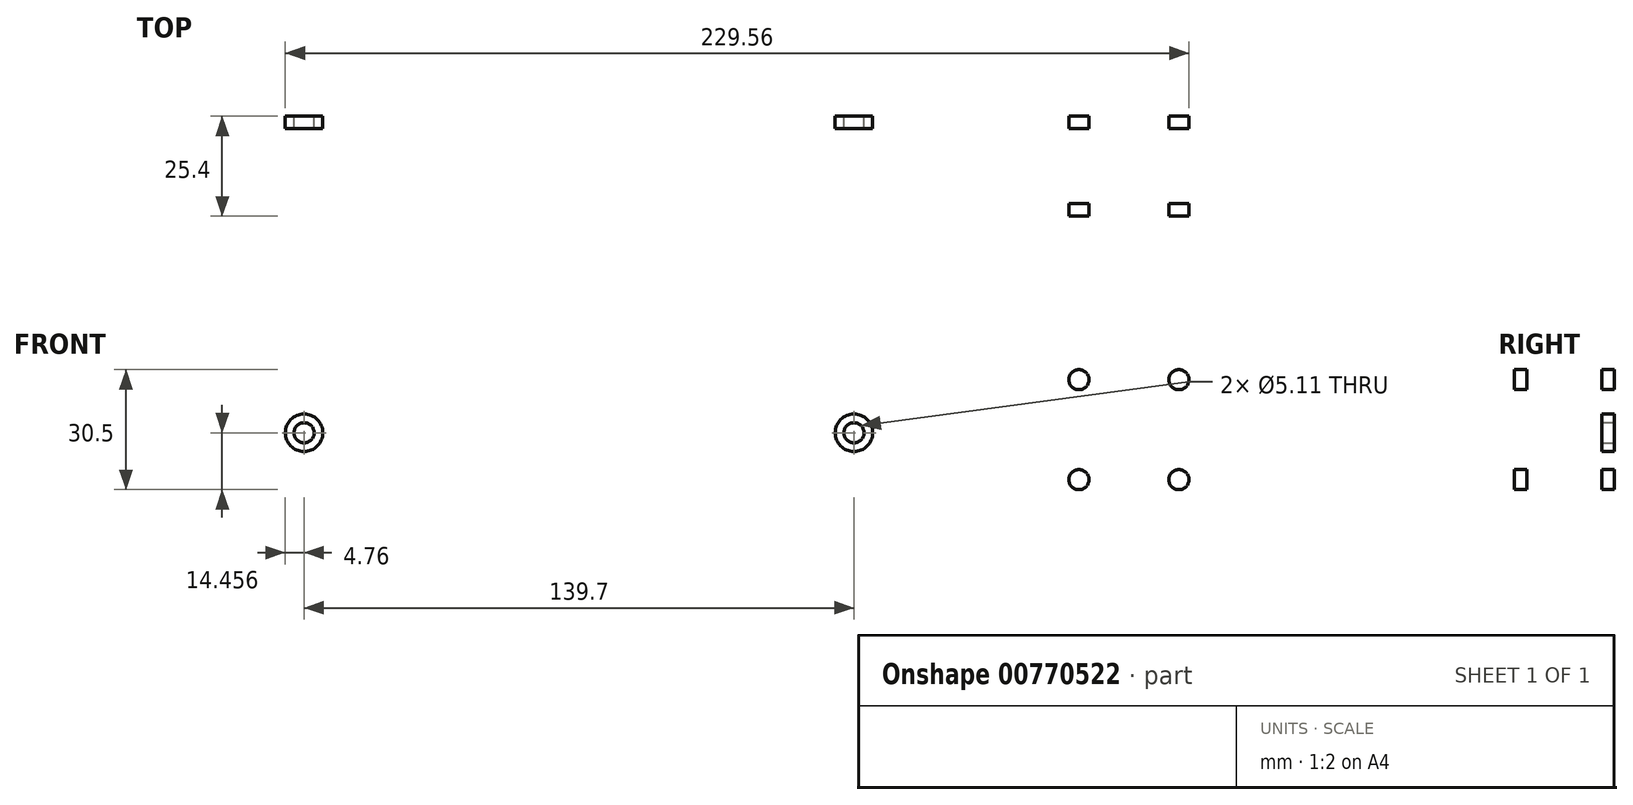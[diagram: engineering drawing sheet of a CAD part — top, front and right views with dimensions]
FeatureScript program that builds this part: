
annotation { "Feature Type Name" : "Feature", "Feature Type Description" : "" }
export const myFeature = defineFeature(function(context is Context, id is Id, definition is map)
    precondition{}
    {
        {
            var Q0;
            Q0=qCreatedBy(makeId("Front.planeOp"),FACE);
            var sketch = newSketch(context, id + "F0", { "sketchPlane" : qUnion([Q0])});
            skLineSegment(sketch, "E0.bottom", {"start": v(381, -25.4) * mm, "end": v(-381, -25.4) * mm});
            skLineSegment(sketch, "E0.top", {"start": v(381, 25.4) * mm, "end": v(-381, 25.4) * mm});
            skLineSegment(sketch, "E0.left", {"start": v(381, -25.4) * mm, "end": v(381, 25.4) * mm});
            skLineSegment(sketch, "E0.right", {"start": v(-381, -25.4) * mm, "end": v(-381, 25.4) * mm});
            skPoint(sketch, "E0.middle", {"position": v(0, 0) * mm});
            skLineSegment(sketch, "E1", {"start": v(-381, 0.8) * mm, "end": v(381, 0.8) * mm, "construction": true});
            skLineSegment(sketch, "E2", {"start": v(-381, -0.8) * mm, "end": v(381, -0.8) * mm, "construction": true});
            skLineSegment(sketch, "E3", {"start": v(0, 0.8) * mm, "end": v(0, -0.8) * mm, "construction": true});
            skCircle(sketch, "E4", {"center": v(-292.1, 0.8) * mm, "radius": 50.8 * mm, "construction": true});
            skCircle(sketch, "E5", {"center": v(292.1, 0.8) * mm, "radius": 50.8 * mm, "construction": true});
            skCircle(sketch, "E6", {"center": v(0, -0.8) * mm, "radius": 50.8 * mm, "construction": true});
            skLineSegment(sketch, "E7", {"start": v(-292.1, 0.8) * mm, "end": v(292.1, 0.8) * mm, "construction": true});
            skCircle(sketch, "E8", {"center": v(0, -0.8) * mm, "radius": 19.11 * mm});
            skCircle(sketch, "E9", {"center": v(-23.81, -0.8) * mm, "radius": 2.55 * mm});
            skCircle(sketch, "E10", {"center": v(23.81, -0.8) * mm, "radius": 2.55 * mm});
            skLineSegment(sketch, "E11", {"start": v(-23.81, -0.8) * mm, "end": v(23.81, -0.8) * mm});
            skLineSegment(sketch, "E12", {"start": v(23.81, -0.8) * mm, "end": v(-23.81, -0.8) * mm, "construction": true});
            skLineSegment(sketch, "E13.bottom", {"start": v(-273.05, -16.68) * mm, "end": v(-311.15, -16.68) * mm});
            skLineSegment(sketch, "E13.top", {"start": v(-273.05, 18.27) * mm, "end": v(-311.15, 18.27) * mm});
            skLineSegment(sketch, "E13.left", {"start": v(-269.88, -16.68) * mm, "end": v(-269.88, 18.27) * mm, "construction": true});
            skLineSegment(sketch, "E13.right", {"start": v(-314.33, -16.68) * mm, "end": v(-314.33, 18.27) * mm, "construction": true});
            skLineSegment(sketch, "E14", {"start": v(-314.33, 15.1) * mm, "end": v(-314.33, 3.35) * mm});
            skLineSegment(sketch, "E15", {"start": v(-314.33, 3.35) * mm, "end": v(-323.85, 3.35) * mm});
            skArc(sketch, "E16", {"start": v(-323.85, 3.35) * mm, "mid": v(-326.4, 0.8) * mm, "end": v(-323.85, -1.76) * mm});
            skLineSegment(sketch, "E17", {"start": v(-323.85, -1.76) * mm, "end": v(-314.33, -1.76) * mm});
            skLineSegment(sketch, "E18", {"start": v(-314.33, -1.76) * mm, "end": v(-314.33, -13.5) * mm});
            skLineSegment(sketch, "E19", {"start": v(-269.88, 3.35) * mm, "end": v(-260.35, 3.35) * mm});
            skLineSegment(sketch, "E20", {"start": v(-269.88, -1.76) * mm, "end": v(-260.35, -1.76) * mm});
            skArc(sketch, "E21", {"start": v(-260.35, -1.76) * mm, "mid": v(-257.8, 0.8) * mm, "end": v(-260.35, 3.35) * mm});
            skCircle(sketch, "E22", {"center": v(-247.65, 0.8) * mm, "radius": 2.55 * mm});
            skLineSegment(sketch, "E23", {"start": v(-269.88, 15.1) * mm, "end": v(-269.88, 3.35) * mm});
            skLineSegment(sketch, "E24", {"start": v(-269.88, -1.76) * mm, "end": v(-269.88, -13.5) * mm});
            skPoint(sketch, "E25.visualSharp", {"position": v(-314.33, 18.27) * mm});
            skArc(sketch, "E25.filletArc", {"start": v(-311.15, 18.27) * mm, "mid": v(-313.4, 17.34) * mm, "end": v(-314.33, 15.1) * mm});
            skPoint(sketch, "E26.visualSharp", {"position": v(-269.88, 18.27) * mm});
            skArc(sketch, "E26.filletArc", {"start": v(-269.88, 15.1) * mm, "mid": v(-270.8, 17.34) * mm, "end": v(-273.05, 18.27) * mm});
            skPoint(sketch, "E27.visualSharp", {"position": v(-269.88, -16.68) * mm});
            skArc(sketch, "E27.filletArc", {"start": v(-273.05, -16.68) * mm, "mid": v(-270.8, -15.75) * mm, "end": v(-269.88, -13.5) * mm});
            skPoint(sketch, "E28.visualSharp", {"position": v(-314.33, -16.68) * mm});
            skArc(sketch, "E28.filletArc", {"start": v(-314.33, -13.5) * mm, "mid": v(-313.4, -15.75) * mm, "end": v(-311.15, -16.68) * mm});
            skArc(sketch, "E29.MirrorCS", {"start": v(311.15, 18.27) * mm, "mid": v(313.4, 17.34) * mm, "end": v(314.33, 15.1) * mm});
            skArc(sketch, "E30.MirrorCS", {"start": v(323.85, 3.35) * mm, "mid": v(326.4, 0.8) * mm, "end": v(323.85, -1.76) * mm});
            skArc(sketch, "E31.MirrorCS", {"start": v(269.88, 15.1) * mm, "mid": v(270.8, 17.34) * mm, "end": v(273.05, 18.27) * mm});
            skArc(sketch, "E32.MirrorCS", {"start": v(314.33, -13.5) * mm, "mid": v(313.4, -15.75) * mm, "end": v(311.15, -16.68) * mm});
            skLineSegment(sketch, "E33.MirrorCS", {"start": v(314.33, 3.35) * mm, "end": v(323.85, 3.35) * mm});
            skLineSegment(sketch, "E34.MirrorCS", {"start": v(323.85, -1.76) * mm, "end": v(314.33, -1.76) * mm});
            skArc(sketch, "E35.MirrorCS", {"start": v(260.35, -1.76) * mm, "mid": v(257.8, 0.8) * mm, "end": v(260.35, 3.35) * mm});
            skArc(sketch, "E36.MirrorCS", {"start": v(273.05, -16.68) * mm, "mid": v(270.8, -15.75) * mm, "end": v(269.88, -13.5) * mm});
            skLineSegment(sketch, "E37.MirrorCS", {"start": v(269.88, 3.35) * mm, "end": v(260.35, 3.35) * mm});
            skCircle(sketch, "E38.MirrorC", {"center": v(247.65, 0.8) * mm, "radius": 2.55 * mm});
            skLineSegment(sketch, "E39.MirrorCS", {"start": v(314.33, -1.76) * mm, "end": v(314.33, -13.5) * mm});
            skLineSegment(sketch, "E40.MirrorCS", {"start": v(269.88, 15.1) * mm, "end": v(269.88, 3.35) * mm});
            skLineSegment(sketch, "E41.MirrorCS", {"start": v(314.33, 15.1) * mm, "end": v(314.33, 3.35) * mm});
            skLineSegment(sketch, "E42.MirrorCS", {"start": v(269.88, -1.76) * mm, "end": v(269.88, -13.5) * mm});
            skPoint(sketch, "E43.MirrorP", {"position": v(314.33, 18.27) * mm});
            skLineSegment(sketch, "E44.MirrorCS", {"start": v(269.88, -1.76) * mm, "end": v(260.35, -1.76) * mm});
            skPoint(sketch, "E45.MirrorP", {"position": v(314.33, -16.68) * mm});
            skLineSegment(sketch, "E46.MirrorCS", {"start": v(269.88, -16.68) * mm, "end": v(269.88, 18.27) * mm, "construction": true});
            skLineSegment(sketch, "E47.MirrorCS", {"start": v(314.33, -16.68) * mm, "end": v(314.33, 18.27) * mm, "construction": true});
            skPoint(sketch, "E48.MirrorP", {"position": v(269.88, 18.27) * mm});
            skLineSegment(sketch, "E49.MirrorCS", {"start": v(273.05, -16.68) * mm, "end": v(311.15, -16.68) * mm});
            skPoint(sketch, "E50.MirrorP", {"position": v(269.88, -16.68) * mm});
            skLineSegment(sketch, "E51.MirrorCS", {"start": v(273.05, 18.27) * mm, "end": v(311.15, 18.27) * mm});
            skCircle(sketch, "E52", {"center": v(69.85, -0.8) * mm, "radius": 2.55 * mm});
            skCircle(sketch, "E53", {"center": v(-69.85, -0.8) * mm, "radius": 2.55 * mm});
            skLineSegment(sketch, "E54", {"start": v(-69.85, -0.8) * mm, "end": v(69.85, -0.8) * mm, "construction": true});
            skSolve(sketch);
        }
        {
            var Q0;
            Q0 = qSketchRegion(id + "F0", true);
            extrude(context, id + "F1", {"entities" : qUnion([Q0]), "depth" : 25.4 * mm, "offsetDistance" : 25.4 * mm});
        }
        {
            var Q0;
            Q0=makeQuery(id+"F1.opExtrude","SWEPT_FACE",FACE,{"disambiguationData":[OSD([sQuery(id+"F0.wireOp",EDGE,"E0.right")])]});
            var sketch = newSketch(context, id + "F2", { "sketchPlane" : qUnion([Q0])});
            skLineSegment(sketch, "E55.0", {"start": v(22.23, 22.23) * mm, "end": v(3.18, 22.23) * mm});
            skLineSegment(sketch, "E55.1", {"start": v(22.23, -22.22) * mm, "end": v(22.23, 22.23) * mm});
            skLineSegment(sketch, "E55.2", {"start": v(22.23, -22.22) * mm, "end": v(3.18, -22.22) * mm});
            skLineSegment(sketch, "E55.3", {"start": v(3.18, -22.22) * mm, "end": v(3.18, 22.23) * mm});
            skSolve(sketch);
        }
        {
            var Q0;
            Q0=makeQuery(id+"F2.imprint","IMPRINT",FACE,{"disambiguationData":[TD([[makeQuery(id+"F2.imprint","IMPRINT",EDGE,{"derivedFrom":sQuery(id+"F2.wireOp",EDGE,"E55.0")}),1.0]])]});
            extrude(context, id + "F3", {"entities" : qUnion([Q0]), "operationType" : NewBodyOperationType.REMOVE, "oppositeDirection" : true, "depth" : 762 * mm, "offsetDistance" : 25.4 * mm});
        }
        {
            var Q0;
            Q0=makeQuery(id+"F1.opExtrude","SWEPT_FACE",FACE,{"disambiguationData":[OSD([sQuery(id+"F0.wireOp",EDGE,"E0.top")])]});
            var sketch = newSketch(context, id + "F4", { "sketchPlane" : qUnion([Q0])});
            skCircle(sketch, "E56", {"center": v(-368.3, -12.7) * mm, "radius": 2.55 * mm});
            skPoint(sketch, "E56.centerSnap0", {"position": v(-381, -12.7) * mm});
            skCircle(sketch, "E57.1.0.0", {"center": v(-342.9, -12.7) * mm, "radius": 2.55 * mm});
            skCircle(sketch, "E57.2.0.0", {"center": v(-317.5, -12.7) * mm, "radius": 2.55 * mm});
            skCircle(sketch, "E57.3.0.0", {"center": v(-292.1, -12.7) * mm, "radius": 2.55 * mm});
            skCircle(sketch, "E57.4.0.0", {"center": v(-266.7, -12.7) * mm, "radius": 2.55 * mm});
            skCircle(sketch, "E57.5.0.0", {"center": v(-241.3, -12.7) * mm, "radius": 2.55 * mm});
            skCircle(sketch, "E57.6.0.0", {"center": v(-215.9, -12.7) * mm, "radius": 2.55 * mm});
            skCircle(sketch, "E57.7.0.0", {"center": v(-190.5, -12.7) * mm, "radius": 2.55 * mm});
            skCircle(sketch, "E57.8.0.0", {"center": v(-165.1, -12.7) * mm, "radius": 2.55 * mm});
            skCircle(sketch, "E57.9.0.0", {"center": v(-139.7, -12.7) * mm, "radius": 2.55 * mm});
            skCircle(sketch, "E57.10.0.0", {"center": v(-114.3, -12.7) * mm, "radius": 2.55 * mm});
            skCircle(sketch, "E57.11.0.0", {"center": v(-88.9, -12.7) * mm, "radius": 2.55 * mm});
            skCircle(sketch, "E57.12.0.0", {"center": v(-63.5, -12.7) * mm, "radius": 2.55 * mm});
            skCircle(sketch, "E57.13.0.0", {"center": v(-38.1, -12.7) * mm, "radius": 2.55 * mm});
            skCircle(sketch, "E57.14.0.0", {"center": v(-12.7, -12.7) * mm, "radius": 2.55 * mm});
            skCircle(sketch, "E57.15.0.0", {"center": v(12.7, -12.7) * mm, "radius": 2.55 * mm});
            skCircle(sketch, "E57.16.0.0", {"center": v(38.1, -12.7) * mm, "radius": 2.55 * mm});
            skCircle(sketch, "E57.17.0.0", {"center": v(63.5, -12.7) * mm, "radius": 2.55 * mm});
            skCircle(sketch, "E57.18.0.0", {"center": v(88.9, -12.7) * mm, "radius": 2.55 * mm});
            skCircle(sketch, "E57.19.0.0", {"center": v(114.3, -12.7) * mm, "radius": 2.55 * mm});
            skCircle(sketch, "E57.20.0.0", {"center": v(139.7, -12.7) * mm, "radius": 2.55 * mm});
            skCircle(sketch, "E57.21.0.0", {"center": v(165.1, -12.7) * mm, "radius": 2.55 * mm});
            skCircle(sketch, "E57.22.0.0", {"center": v(190.5, -12.7) * mm, "radius": 2.55 * mm});
            skCircle(sketch, "E57.23.0.0", {"center": v(215.9, -12.7) * mm, "radius": 2.55 * mm});
            skCircle(sketch, "E57.24.0.0", {"center": v(241.3, -12.7) * mm, "radius": 2.55 * mm});
            skCircle(sketch, "E57.25.0.0", {"center": v(266.7, -12.7) * mm, "radius": 2.55 * mm});
            skCircle(sketch, "E57.26.0.0", {"center": v(292.1, -12.7) * mm, "radius": 2.55 * mm});
            skCircle(sketch, "E57.27.0.0", {"center": v(317.5, -12.7) * mm, "radius": 2.55 * mm});
            skCircle(sketch, "E57.28.0.0", {"center": v(342.9, -12.7) * mm, "radius": 2.55 * mm});
            skCircle(sketch, "E57.29.0.0", {"center": v(368.3, -12.7) * mm, "radius": 2.55 * mm});
            skLineSegment(sketch, "E57.direction1", {"start": v(-368.3, -12.7) * mm, "end": v(-342.9, -12.7) * mm, "construction": true});
            skSolve(sketch);
        }
        {
            var Q0;
            Q0=sQuery(id+"F4.wireOp",VERTEX,"E57.22.0.0.center");
            var Q1;
            Q1=sQuery(id+"F4.wireOp",VERTEX,"E57.16.0.0.center");
            var Q2;
            Q2=sQuery(id+"F4.wireOp",VERTEX,"E57.23.0.0.center");
            var Q3;
            Q3=sQuery(id+"F4.wireOp",VERTEX,"E57.17.0.0.center");
            var Q4;
            Q4=sQuery(id+"F4.wireOp",VERTEX,"E57.26.0.0.center");
            var Q5;
            Q5=sQuery(id+"F4.wireOp",VERTEX,"E57.20.0.0.center");
            var Q6;
            Q6=sQuery(id+"F4.wireOp",VERTEX,"E57.13.0.0.center");
            var Q7;
            Q7=sQuery(id+"F4.wireOp",VERTEX,"E57.29.0.0.center");
            var Q8;
            Q8=sQuery(id+"F4.wireOp",VERTEX,"E57.24.0.0.center");
            var Q9;
            Q9=sQuery(id+"F4.wireOp",VERTEX,"E57.10.0.0.center");
            var Q10;
            Q10=sQuery(id+"F4.wireOp",VERTEX,"E57.18.0.0.center");
            var Q11;
            Q11=sQuery(id+"F4.wireOp",VERTEX,"E57.11.0.0.center");
            var Q12;
            Q12=sQuery(id+"F4.wireOp",VERTEX,"E57.27.0.0.center");
            var Q13;
            Q13=sQuery(id+"F4.wireOp",VERTEX,"E57.12.0.0.center");
            var Q14;
            Q14=sQuery(id+"F4.wireOp",VERTEX,"E57.14.0.0.center");
            var Q15;
            Q15=sQuery(id+"F4.wireOp",VERTEX,"E57.1.0.0.center");
            var Q16;
            Q16=sQuery(id+"F4.wireOp",VERTEX,"E57.2.0.0.center");
            var Q17;
            Q17=sQuery(id+"F4.wireOp",VERTEX,"E57.3.0.0.center");
            var Q18;
            Q18=sQuery(id+"F4.wireOp",VERTEX,"E57.4.0.0.center");
            var Q19;
            Q19=sQuery(id+"F4.wireOp",VERTEX,"E57.5.0.0.center");
            var Q20;
            Q20=sQuery(id+"F4.wireOp",VERTEX,"E57.6.0.0.center");
            var Q21;
            Q21=sQuery(id+"F4.wireOp",VERTEX,"E57.7.0.0.center");
            var Q22;
            Q22=sQuery(id+"F4.wireOp",VERTEX,"E57.8.0.0.center");
            var Q23;
            Q23=sQuery(id+"F4.wireOp",VERTEX,"E57.9.0.0.center");
            var Q24;
            Q24=sQuery(id+"F4.wireOp",VERTEX,"E57.25.0.0.center");
            var Q25;
            Q25=sQuery(id+"F4.wireOp",VERTEX,"E57.21.0.0.center");
            var Q26;
            Q26=sQuery(id+"F4.wireOp",VERTEX,"E57.19.0.0.center");
            var Q27;
            Q27=sQuery(id+"F4.wireOp",VERTEX,"E57.28.0.0.center");
            var Q28;
            Q28=sQuery(id+"F4.wireOp",VERTEX,"E57.15.0.0.center");
            var Q29;
            Q29=sQuery(id+"F4.wireOp",VERTEX,"E56.center");
            var Q30;
            Q30=makeQuery(id+"F1.opExtrude","SWEPT_BODY",BODY,{"disambiguationData":[OSD([sQuery(id+"F0.wireOp",EDGE,"E0.bottom"),sQuery(id+"F0.wireOp",EDGE,"E0.top"),sQuery(id+"F0.wireOp",EDGE,"E0.right"),sQuery(id+"F0.wireOp",EDGE,"E8"),sQuery(id+"F0.wireOp",EDGE,"E9"),sQuery(id+"F0.wireOp",EDGE,"E10"),sQuery(id+"F0.wireOp",EDGE,"E13.bottom"),sQuery(id+"F0.wireOp",EDGE,"E13.top"),sQuery(id+"F0.wireOp",EDGE,"E14"),sQuery(id+"F0.wireOp",EDGE,"E15"),sQuery(id+"F0.wireOp",EDGE,"E16"),sQuery(id+"F0.wireOp",EDGE,"E17"),sQuery(id+"F0.wireOp",EDGE,"E18"),sQuery(id+"F0.wireOp",EDGE,"E19"),sQuery(id+"F0.wireOp",EDGE,"E20"),sQuery(id+"F0.wireOp",EDGE,"E21"),sQuery(id+"F0.wireOp",EDGE,"E22"),sQuery(id+"F0.wireOp",EDGE,"E23"),sQuery(id+"F0.wireOp",EDGE,"E24"),sQuery(id+"F0.wireOp",EDGE,"E25.filletArc"),sQuery(id+"F0.wireOp",EDGE,"E26.filletArc"),sQuery(id+"F0.wireOp",EDGE,"E27.filletArc"),sQuery(id+"F0.wireOp",EDGE,"E28.filletArc"),sQuery(id+"F0.wireOp",EDGE,"E29.MirrorCS"),sQuery(id+"F0.wireOp",EDGE,"E30.MirrorCS"),sQuery(id+"F0.wireOp",EDGE,"E31.MirrorCS"),sQuery(id+"F0.wireOp",EDGE,"E32.MirrorCS"),sQuery(id+"F0.wireOp",EDGE,"E33.MirrorCS"),sQuery(id+"F0.wireOp",EDGE,"E34.MirrorCS"),sQuery(id+"F0.wireOp",EDGE,"E35.MirrorCS"),sQuery(id+"F0.wireOp",EDGE,"E36.MirrorCS"),sQuery(id+"F0.wireOp",EDGE,"E37.MirrorCS"),sQuery(id+"F0.wireOp",EDGE,"E38.MirrorC"),sQuery(id+"F0.wireOp",EDGE,"E39.MirrorCS"),sQuery(id+"F0.wireOp",EDGE,"E40.MirrorCS"),sQuery(id+"F0.wireOp",EDGE,"E41.MirrorCS"),sQuery(id+"F0.wireOp",EDGE,"E42.MirrorCS"),sQuery(id+"F0.wireOp",EDGE,"E44.MirrorCS"),sQuery(id+"F0.wireOp",EDGE,"E49.MirrorCS"),sQuery(id+"F0.wireOp",EDGE,"E51.MirrorCS"),sQuery(id+"F0.wireOp",EDGE,"E0.left"),sQuery(id+"F0.wireOp",EDGE,"E52"),sQuery(id+"F0.wireOp",EDGE,"E53")])]});
            hole(context, id + "F5", {"style" : HoleStyle.SIMPLE, "endStyle" : HoleEndStyle.BLIND, "holeDiameter" : 5.1 * mm, "majorDiameter" : 6.35 * mm, "holeDepth" : 50.8 * mm, "isTappedThrough" : true, "tappedDepth" : 12.7 * mm, "tapClearance" : 3, "startFromSketch" : true, "locations" : qUnion([Q0, Q1, Q2, Q3, Q4, Q5, Q6, Q7, Q8, Q9, Q10, Q11, Q12, Q13, Q14, Q15, Q16, Q17, Q18, Q19, Q20, Q21, Q22, Q23, Q24, Q25, Q26, Q27, Q28, Q29]), "scope" : qUnion([Q30])});
        }
        {
            var Q0;
            Q0=makeQuery(id+"F1.opExtrude","CAP_FACE",FACE,{"disambiguationData":[OSD([sQuery(id+"F0.wireOp",EDGE,"E0.bottom"),sQuery(id+"F0.wireOp",EDGE,"E0.top"),sQuery(id+"F0.wireOp",EDGE,"E0.right"),sQuery(id+"F0.wireOp",EDGE,"E8"),sQuery(id+"F0.wireOp",EDGE,"E9"),sQuery(id+"F0.wireOp",EDGE,"E10"),sQuery(id+"F0.wireOp",EDGE,"E13.bottom"),sQuery(id+"F0.wireOp",EDGE,"E13.top"),sQuery(id+"F0.wireOp",EDGE,"E14"),sQuery(id+"F0.wireOp",EDGE,"E15"),sQuery(id+"F0.wireOp",EDGE,"E16"),sQuery(id+"F0.wireOp",EDGE,"E17"),sQuery(id+"F0.wireOp",EDGE,"E18"),sQuery(id+"F0.wireOp",EDGE,"E19"),sQuery(id+"F0.wireOp",EDGE,"E20"),sQuery(id+"F0.wireOp",EDGE,"E21"),sQuery(id+"F0.wireOp",EDGE,"E22"),sQuery(id+"F0.wireOp",EDGE,"E23"),sQuery(id+"F0.wireOp",EDGE,"E24"),sQuery(id+"F0.wireOp",EDGE,"E25.filletArc"),sQuery(id+"F0.wireOp",EDGE,"E26.filletArc"),sQuery(id+"F0.wireOp",EDGE,"E27.filletArc"),sQuery(id+"F0.wireOp",EDGE,"E28.filletArc"),sQuery(id+"F0.wireOp",EDGE,"E29.MirrorCS"),sQuery(id+"F0.wireOp",EDGE,"E30.MirrorCS"),sQuery(id+"F0.wireOp",EDGE,"E31.MirrorCS"),sQuery(id+"F0.wireOp",EDGE,"E32.MirrorCS"),sQuery(id+"F0.wireOp",EDGE,"E33.MirrorCS"),sQuery(id+"F0.wireOp",EDGE,"E34.MirrorCS"),sQuery(id+"F0.wireOp",EDGE,"E35.MirrorCS"),sQuery(id+"F0.wireOp",EDGE,"E36.MirrorCS"),sQuery(id+"F0.wireOp",EDGE,"E37.MirrorCS"),sQuery(id+"F0.wireOp",EDGE,"E38.MirrorC"),sQuery(id+"F0.wireOp",EDGE,"E39.MirrorCS"),sQuery(id+"F0.wireOp",EDGE,"E40.MirrorCS"),sQuery(id+"F0.wireOp",EDGE,"E41.MirrorCS"),sQuery(id+"F0.wireOp",EDGE,"E42.MirrorCS"),sQuery(id+"F0.wireOp",EDGE,"E44.MirrorCS"),sQuery(id+"F0.wireOp",EDGE,"E49.MirrorCS"),sQuery(id+"F0.wireOp",EDGE,"E51.MirrorCS"),sQuery(id+"F0.wireOp",EDGE,"E0.left"),sQuery(id+"F0.wireOp",EDGE,"E52"),sQuery(id+"F0.wireOp",EDGE,"E53")])],"isStart":false});
            var sketch = newSketch(context, id + "F6", { "sketchPlane" : qUnion([Q0])});
            skCircle(sketch, "E58", {"center": v(-69.85, -0.8) * mm, "radius": 4.76 * mm});
            skCircle(sketch, "E59", {"center": v(69.85, -0.8) * mm, "radius": 4.76 * mm});
            skSolve(sketch);
        }
        {
            var Q0;
            Q0=sQuery(id+"F6.wireOp",VERTEX,"E58.center");
            var Q1;
            Q1=sQuery(id+"F6.wireOp",VERTEX,"E59.center");
            var Q2;
            Q2=makeQuery(id+"F1.opExtrude","SWEPT_BODY",BODY,{"disambiguationData":[OSD([sQuery(id+"F0.wireOp",EDGE,"E0.bottom"),sQuery(id+"F0.wireOp",EDGE,"E0.top"),sQuery(id+"F0.wireOp",EDGE,"E0.right"),sQuery(id+"F0.wireOp",EDGE,"E8"),sQuery(id+"F0.wireOp",EDGE,"E9"),sQuery(id+"F0.wireOp",EDGE,"E10"),sQuery(id+"F0.wireOp",EDGE,"E13.bottom"),sQuery(id+"F0.wireOp",EDGE,"E13.top"),sQuery(id+"F0.wireOp",EDGE,"E14"),sQuery(id+"F0.wireOp",EDGE,"E15"),sQuery(id+"F0.wireOp",EDGE,"E16"),sQuery(id+"F0.wireOp",EDGE,"E17"),sQuery(id+"F0.wireOp",EDGE,"E18"),sQuery(id+"F0.wireOp",EDGE,"E19"),sQuery(id+"F0.wireOp",EDGE,"E20"),sQuery(id+"F0.wireOp",EDGE,"E21"),sQuery(id+"F0.wireOp",EDGE,"E22"),sQuery(id+"F0.wireOp",EDGE,"E23"),sQuery(id+"F0.wireOp",EDGE,"E24"),sQuery(id+"F0.wireOp",EDGE,"E25.filletArc"),sQuery(id+"F0.wireOp",EDGE,"E26.filletArc"),sQuery(id+"F0.wireOp",EDGE,"E27.filletArc"),sQuery(id+"F0.wireOp",EDGE,"E28.filletArc"),sQuery(id+"F0.wireOp",EDGE,"E29.MirrorCS"),sQuery(id+"F0.wireOp",EDGE,"E30.MirrorCS"),sQuery(id+"F0.wireOp",EDGE,"E31.MirrorCS"),sQuery(id+"F0.wireOp",EDGE,"E32.MirrorCS"),sQuery(id+"F0.wireOp",EDGE,"E33.MirrorCS"),sQuery(id+"F0.wireOp",EDGE,"E34.MirrorCS"),sQuery(id+"F0.wireOp",EDGE,"E35.MirrorCS"),sQuery(id+"F0.wireOp",EDGE,"E36.MirrorCS"),sQuery(id+"F0.wireOp",EDGE,"E37.MirrorCS"),sQuery(id+"F0.wireOp",EDGE,"E38.MirrorC"),sQuery(id+"F0.wireOp",EDGE,"E39.MirrorCS"),sQuery(id+"F0.wireOp",EDGE,"E40.MirrorCS"),sQuery(id+"F0.wireOp",EDGE,"E41.MirrorCS"),sQuery(id+"F0.wireOp",EDGE,"E42.MirrorCS"),sQuery(id+"F0.wireOp",EDGE,"E44.MirrorCS"),sQuery(id+"F0.wireOp",EDGE,"E49.MirrorCS"),sQuery(id+"F0.wireOp",EDGE,"E51.MirrorCS"),sQuery(id+"F0.wireOp",EDGE,"E0.left"),sQuery(id+"F0.wireOp",EDGE,"E52"),sQuery(id+"F0.wireOp",EDGE,"E53")])]});
            hole(context, id + "F7", {"style" : HoleStyle.SIMPLE, "endStyle" : HoleEndStyle.BLIND, "holeDiameter" : 9.52 * mm, "majorDiameter" : 6.35 * mm, "holeDepth" : 3.17 * mm, "isTappedThrough" : true, "tappedDepth" : 12.7 * mm, "tapClearance" : 3, "startFromSketch" : true, "locations" : qUnion([Q0, Q1]), "scope" : qUnion([Q2])});
        }
        {
            var Q0;
            Q0=makeQuery(id+"F1.opExtrude","CAP_FACE",FACE,{"disambiguationData":[OSD([sQuery(id+"F0.wireOp",EDGE,"E0.bottom"),sQuery(id+"F0.wireOp",EDGE,"E0.top"),sQuery(id+"F0.wireOp",EDGE,"E0.right"),sQuery(id+"F0.wireOp",EDGE,"E8"),sQuery(id+"F0.wireOp",EDGE,"E9"),sQuery(id+"F0.wireOp",EDGE,"E10"),sQuery(id+"F0.wireOp",EDGE,"E13.bottom"),sQuery(id+"F0.wireOp",EDGE,"E13.top"),sQuery(id+"F0.wireOp",EDGE,"E14"),sQuery(id+"F0.wireOp",EDGE,"E15"),sQuery(id+"F0.wireOp",EDGE,"E16"),sQuery(id+"F0.wireOp",EDGE,"E17"),sQuery(id+"F0.wireOp",EDGE,"E18"),sQuery(id+"F0.wireOp",EDGE,"E19"),sQuery(id+"F0.wireOp",EDGE,"E20"),sQuery(id+"F0.wireOp",EDGE,"E21"),sQuery(id+"F0.wireOp",EDGE,"E22"),sQuery(id+"F0.wireOp",EDGE,"E23"),sQuery(id+"F0.wireOp",EDGE,"E24"),sQuery(id+"F0.wireOp",EDGE,"E25.filletArc"),sQuery(id+"F0.wireOp",EDGE,"E26.filletArc"),sQuery(id+"F0.wireOp",EDGE,"E27.filletArc"),sQuery(id+"F0.wireOp",EDGE,"E28.filletArc"),sQuery(id+"F0.wireOp",EDGE,"E29.MirrorCS"),sQuery(id+"F0.wireOp",EDGE,"E30.MirrorCS"),sQuery(id+"F0.wireOp",EDGE,"E31.MirrorCS"),sQuery(id+"F0.wireOp",EDGE,"E32.MirrorCS"),sQuery(id+"F0.wireOp",EDGE,"E33.MirrorCS"),sQuery(id+"F0.wireOp",EDGE,"E34.MirrorCS"),sQuery(id+"F0.wireOp",EDGE,"E35.MirrorCS"),sQuery(id+"F0.wireOp",EDGE,"E36.MirrorCS"),sQuery(id+"F0.wireOp",EDGE,"E37.MirrorCS"),sQuery(id+"F0.wireOp",EDGE,"E38.MirrorC"),sQuery(id+"F0.wireOp",EDGE,"E39.MirrorCS"),sQuery(id+"F0.wireOp",EDGE,"E40.MirrorCS"),sQuery(id+"F0.wireOp",EDGE,"E41.MirrorCS"),sQuery(id+"F0.wireOp",EDGE,"E42.MirrorCS"),sQuery(id+"F0.wireOp",EDGE,"E44.MirrorCS"),sQuery(id+"F0.wireOp",EDGE,"E49.MirrorCS"),sQuery(id+"F0.wireOp",EDGE,"E51.MirrorCS"),sQuery(id+"F0.wireOp",EDGE,"E0.left"),sQuery(id+"F0.wireOp",EDGE,"E52"),sQuery(id+"F0.wireOp",EDGE,"E53")])],"isStart":false});
            var sketch = newSketch(context, id + "F8", { "sketchPlane" : qUnion([Q0])});
            skLineSegment(sketch, "E60.bottom", {"start": v(-152.4, 12.7) * mm, "end": v(-127, 12.7) * mm, "construction": true});
            skLineSegment(sketch, "E60.top", {"start": v(-152.4, -12.7) * mm, "end": v(-127, -12.7) * mm, "construction": true});
            skLineSegment(sketch, "E60.left", {"start": v(-152.4, 12.7) * mm, "end": v(-152.4, -12.7) * mm, "construction": true});
            skLineSegment(sketch, "E60.right", {"start": v(-127, 12.7) * mm, "end": v(-127, -12.7) * mm, "construction": true});
            skPoint(sketch, "E60.middle", {"position": v(-139.7, 0) * mm});
            skCircle(sketch, "E61", {"center": v(-152.4, 12.7) * mm, "radius": 2.55 * mm});
            skCircle(sketch, "E62", {"center": v(-127, 12.7) * mm, "radius": 2.55 * mm});
            skCircle(sketch, "E63", {"center": v(-152.4, -12.7) * mm, "radius": 2.55 * mm});
            skCircle(sketch, "E64", {"center": v(-127, -12.7) * mm, "radius": 2.55 * mm});
            skLineSegment(sketch, "E65", {"start": v(0, 25.4) * mm, "end": v(0, -25.4) * mm, "construction": true});
            skCircle(sketch, "E66.MirrorC", {"center": v(127, 12.7) * mm, "radius": 2.55 * mm});
            skCircle(sketch, "E67.MirrorC", {"center": v(152.4, -12.7) * mm, "radius": 2.55 * mm});
            skCircle(sketch, "E68.MirrorC", {"center": v(127, -12.7) * mm, "radius": 2.55 * mm});
            skCircle(sketch, "E69.MirrorC", {"center": v(152.4, 12.7) * mm, "radius": 2.55 * mm});
            skLineSegment(sketch, "E70.MirrorCS", {"start": v(127, 12.7) * mm, "end": v(127, -12.7) * mm, "construction": true});
            skLineSegment(sketch, "E71.MirrorCS", {"start": v(152.4, 12.7) * mm, "end": v(127, 12.7) * mm, "construction": true});
            skLineSegment(sketch, "E72.MirrorCS", {"start": v(152.4, 12.7) * mm, "end": v(152.4, -12.7) * mm, "construction": true});
            skPoint(sketch, "E73.MirrorP", {"position": v(139.7, 0) * mm});
            skLineSegment(sketch, "E74.MirrorCS", {"start": v(152.4, -12.7) * mm, "end": v(127, -12.7) * mm, "construction": true});
            skSolve(sketch);
        }
        {
            var Q0;
            Q0=makeQuery(id+"F8.imprint","IMPRINT",FACE,{"disambiguationData":[TD([[makeQuery(id+"F8.imprint","IMPRINT",EDGE,{"derivedFrom":sQuery(id+"F8.wireOp",EDGE,"E63")}),1.0]])]});
            var Q1;
            Q1=makeQuery(id+"F8.imprint","IMPRINT",FACE,{"disambiguationData":[TD([[makeQuery(id+"F8.imprint","IMPRINT",EDGE,{"derivedFrom":sQuery(id+"F8.wireOp",EDGE,"E61")}),1.0]])]});
            var Q2;
            Q2=makeQuery(id+"F8.imprint","IMPRINT",FACE,{"disambiguationData":[TD([[makeQuery(id+"F8.imprint","IMPRINT",EDGE,{"derivedFrom":sQuery(id+"F8.wireOp",EDGE,"E62")}),1.0]])]});
            var Q3;
            Q3=makeQuery(id+"F8.imprint","IMPRINT",FACE,{"disambiguationData":[TD([[makeQuery(id+"F8.imprint","IMPRINT",EDGE,{"derivedFrom":sQuery(id+"F8.wireOp",EDGE,"E64")}),1.0]])]});
            var Q4;
            Q4=makeQuery(id+"F8.imprint","IMPRINT",FACE,{"disambiguationData":[TD([[makeQuery(id+"F8.imprint","IMPRINT",EDGE,{"derivedFrom":sQuery(id+"F8.wireOp",EDGE,"E68.MirrorC")}),-1.0]])]});
            var Q5;
            Q5=makeQuery(id+"F8.imprint","IMPRINT",FACE,{"disambiguationData":[TD([[makeQuery(id+"F8.imprint","IMPRINT",EDGE,{"derivedFrom":sQuery(id+"F8.wireOp",EDGE,"E66.MirrorC")}),-1.0]])]});
            var Q6;
            Q6=makeQuery(id+"F8.imprint","IMPRINT",FACE,{"disambiguationData":[TD([[makeQuery(id+"F8.imprint","IMPRINT",EDGE,{"derivedFrom":sQuery(id+"F8.wireOp",EDGE,"E67.MirrorC")}),-1.0]])]});
            var Q7;
            Q7=makeQuery(id+"F8.imprint","IMPRINT",FACE,{"disambiguationData":[TD([[makeQuery(id+"F8.imprint","IMPRINT",EDGE,{"derivedFrom":sQuery(id+"F8.wireOp",EDGE,"E69.MirrorC")}),-1.0]])]});
            extrude(context, id + "F9", {"entities" : qUnion([Q0, Q1, Q2, Q3, Q4, Q5, Q6, Q7]), "operationType" : NewBodyOperationType.REMOVE, "oppositeDirection" : true, "depth" : 25.4 * mm, "offsetDistance" : 25.4 * mm});
        }
    });
